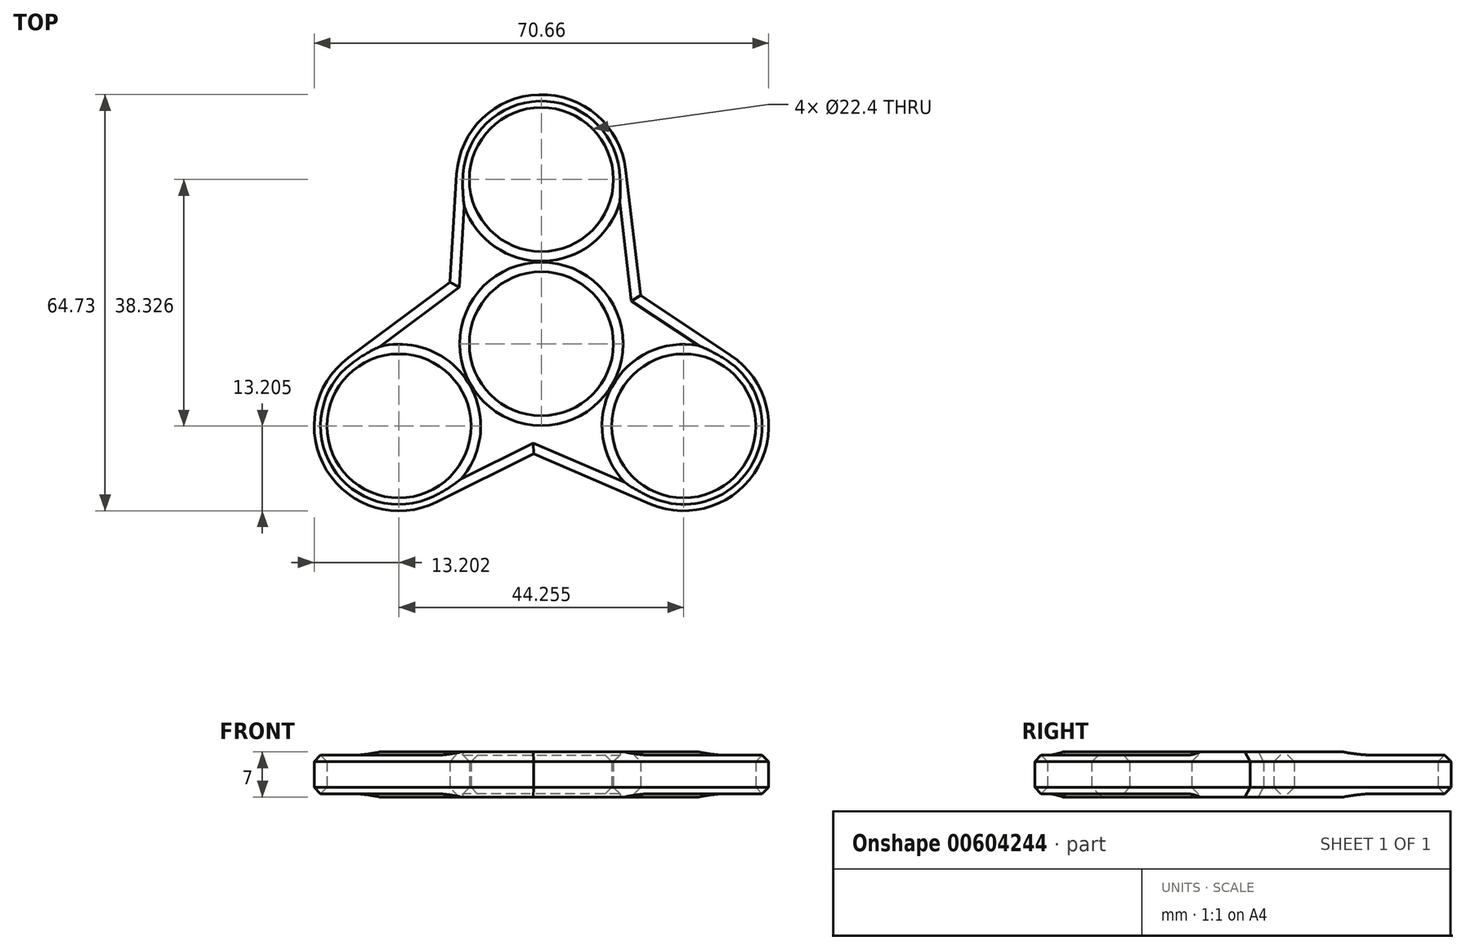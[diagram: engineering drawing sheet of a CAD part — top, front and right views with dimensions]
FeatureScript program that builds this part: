
annotation { "Feature Type Name" : "Feature", "Feature Type Description" : "" }
export const myFeature = defineFeature(function(context is Context, id is Id, definition is map)
    precondition{}
    {
        {
            var Q0;
            Q0=qCreatedBy(makeId("Top.planeOp"),FACE);
            var sketch = newSketch(context, id + "F0", { "sketchPlane" : qUnion([Q0])});
            skCircle(sketch, "E0", {"center": v(0, 0) * mm, "radius": 11.2 * mm});
            skCircle(sketch, "E1", {"center": v(0, 25.55) * mm, "radius": 11.2 * mm});
            skArc(sketch, "E2", {"start": v(13.2, 25.55) * mm, "mid": v(0.41, 38.74) * mm, "end": v(-13.17, 26.37) * mm});
            skCircle(sketch, "E3.1.1", {"center": v(-22.13, -12.78) * mm, "radius": 11.2 * mm});
            skArc(sketch, "E3.2.0", {"start": v(16.9, -24.9) * mm, "mid": v(33.74, -19.06) * mm, "end": v(29.43, -1.78) * mm});
            skCircle(sketch, "E3.2.1", {"center": v(22.13, -12.78) * mm, "radius": 11.2 * mm});
            skLineSegment(sketch, "E3.anchor1", {"start": v(0, 0) * mm, "end": v(0, 11.2) * mm, "construction": true});
            skLineSegment(sketch, "E3.anchor2", {"start": v(0, 0) * mm, "end": v(22.13, -12.78) * mm, "construction": true});
            skLineSegment(sketch, "E4", {"start": v(13.1, 27.1) * mm, "end": v(15.41, 7.52) * mm});
            skLineSegment(sketch, "E5", {"start": v(15.41, 7.52) * mm, "end": v(29.43, -1.78) * mm});
            skLineSegment(sketch, "E6.1.1", {"start": v(-30.02, -2.2) * mm, "end": v(-14.22, 9.59) * mm});
            skLineSegment(sketch, "E6.1.2", {"start": v(-14.22, 9.59) * mm, "end": v(-13.17, 26.37) * mm});
            skLineSegment(sketch, "E6.2.1", {"start": v(16.9, -24.9) * mm, "end": v(-1.2, -17.1) * mm});
            skLineSegment(sketch, "E6.2.2", {"start": v(-1.2, -17.1) * mm, "end": v(-16.25, -24.6) * mm});
            skArc(sketch, "E6.2.3", {"start": v(0, 11.2) * mm, "mid": v(-10.82, 2.9) * mm, "end": v(-5.6, -9.7) * mm});
            skLineSegment(sketch, "E6.anchor2", {"start": v(0, 0) * mm, "end": v(-9.7, -5.6) * mm, "construction": true});
            skArc(sketch, "E7.trimOffspring", {"start": v(-30.02, -2.2) * mm, "mid": v(-33.37, -19.69) * mm, "end": v(-16.25, -24.6) * mm});
            skLineSegment(sketch, "E8.trimOffspring", {"start": v(-12.43, -7.18) * mm, "end": v(-22.13, -12.78) * mm, "construction": true});
            skLineSegment(sketch, "E9.trimOffspring", {"start": v(0, 13.2) * mm, "end": v(0, 25.55) * mm, "construction": true});
            skSolve(sketch);
        }
        {
            var Q0;
            Q0=makeQuery(id+"F0.imprint","IMPRINT",FACE,{"disambiguationData":[TD([[makeQuery(id+"F0.imprint","IMPRINT",EDGE,{"derivedFrom":sQuery(id+"F0.wireOp",EDGE,"E1")}),-1.0]])]});
            extrude(context, id + "F1", {"entities" : qUnion([Q0]), "depth" : 7 * mm, "offsetDistance" : 25 * mm});
        }
        {
            var Q0;
            Q0=makeQuery(id+"F1.opExtrude","CAP_FACE",FACE,{"disambiguationData":[OSD([sQuery(id+"F0.wireOp",EDGE,"E1"),sQuery(id+"F0.wireOp",EDGE,"E3.2.0"),sQuery(id+"F0.wireOp",EDGE,"E4"),sQuery(id+"F0.wireOp",EDGE,"E5"),sQuery(id+"F0.wireOp",EDGE,"E3.1.1"),sQuery(id+"F0.wireOp",EDGE,"E6.1.1"),sQuery(id+"F0.wireOp",EDGE,"E6.1.2"),sQuery(id+"F0.wireOp",EDGE,"E0"),sQuery(id+"F0.wireOp",EDGE,"E2"),sQuery(id+"F0.wireOp",EDGE,"E3.2.1"),sQuery(id+"F0.wireOp",EDGE,"E6.2.1"),sQuery(id+"F0.wireOp",EDGE,"E6.2.2"),sQuery(id+"F0.wireOp",EDGE,"E7.trimOffspring")])],"isStart":false});
            chamfer(context, id + "F2", {"entities" : qUnion([Q0]), "width" : 1.5 * mm, "tangentPropagation" : true});
        }
        {
            var Q0;
            Q0=makeQuery(id+"F1.opExtrude","CAP_FACE",FACE,{"disambiguationData":[OSD([sQuery(id+"F0.wireOp",EDGE,"E1"),sQuery(id+"F0.wireOp",EDGE,"E3.2.0"),sQuery(id+"F0.wireOp",EDGE,"E4"),sQuery(id+"F0.wireOp",EDGE,"E5"),sQuery(id+"F0.wireOp",EDGE,"E3.1.1"),sQuery(id+"F0.wireOp",EDGE,"E6.1.1"),sQuery(id+"F0.wireOp",EDGE,"E6.1.2"),sQuery(id+"F0.wireOp",EDGE,"E0"),sQuery(id+"F0.wireOp",EDGE,"E2"),sQuery(id+"F0.wireOp",EDGE,"E3.2.1"),sQuery(id+"F0.wireOp",EDGE,"E6.2.1"),sQuery(id+"F0.wireOp",EDGE,"E6.2.2"),sQuery(id+"F0.wireOp",EDGE,"E7.trimOffspring")])],"isStart":true});
            chamfer(context, id + "F3", {"entities" : qUnion([Q0]), "width" : 1.5 * mm, "tangentPropagation" : true});
        }
    });
